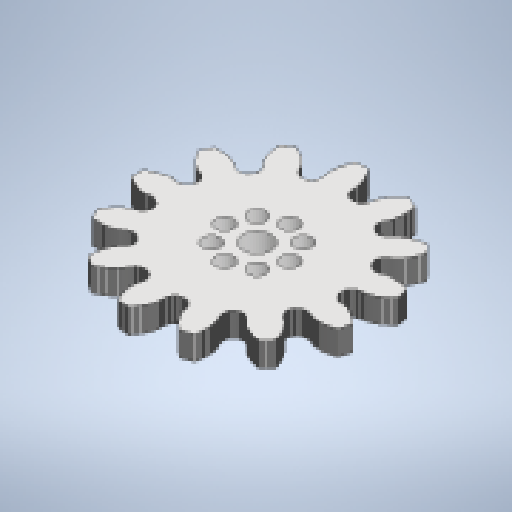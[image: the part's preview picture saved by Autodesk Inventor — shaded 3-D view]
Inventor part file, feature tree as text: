
AUTODESK INVENTOR PART (.ipt)
format: ipt  version: 2024 (Build 280153000, 153)  size: 2,073,600 bytes
history: native  units: mm
features: other x6, extrude x5, sketch x4, reference x1
ambient origin geometry x8: Origin, YZ Plane, XZ Plane, XY Plane, X Axis, Y Axis, Z Axis, Center Point
bodies: Body1 (feature_tree)
feature tree (16):
  other  "作業平面1"
  sketch  "スケッチ5"
  extrude  "押し出し5"  Depth=3.5mm
  extrude  "押し出し6"  TaperAngle=0.0deg  [1 undecoded]
  extrude  "押し出し4"  Depth=130.0mm TaperAngle=360.0deg
  extrude  "押し出し7"  Depth=3.0mm TaperAngle=0.0deg
  extrude  "押し出し8"  Depth=3.0mm TaperAngle=0.0deg
  sketch  "スケッチ4"
  other  "ソリッド3"
  sketch  "スケッチ6"
  reference  "参照1"
  sketch  "スケッチ7"
  other  "<userpath>\OneDrive\ドキュメント\Inventor\Vixen\kosi.iam"
  other  "kosi.iam"
  other  "かさ歯車:1"
  other  "かさ歯車2:1"
note: 1 required parameter value undecoded (feature->parameter linkage not recoverable at this tier; creation-order binding heuristic only, values carry confidence <= 0.55)
